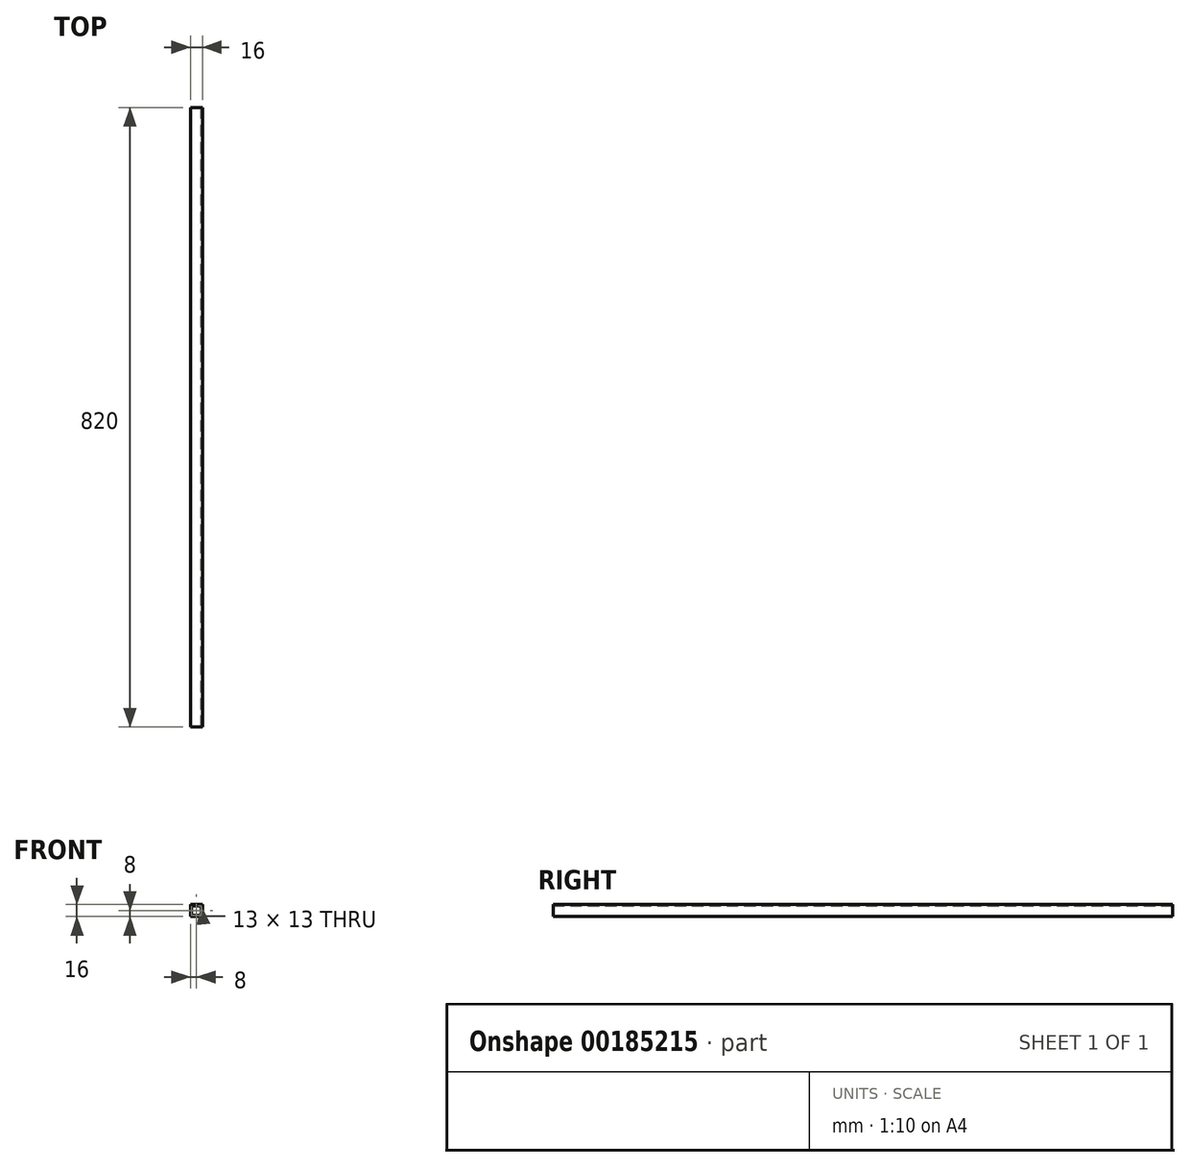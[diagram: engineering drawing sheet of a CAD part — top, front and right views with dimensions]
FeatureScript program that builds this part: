
annotation { "Feature Type Name" : "Feature", "Feature Type Description" : "" }
export const myFeature = defineFeature(function(context is Context, id is Id, definition is map)
    precondition{}
    {
        {
            var Q0;
            Q0=qCreatedBy(makeId("Front.planeOp"),FACE);
            var sketch = newSketch(context, id + "F0", { "sketchPlane" : qUnion([Q0])});
            skLineSegment(sketch, "E0.bottom", {"start": v(8, 8) * mm, "end": v(-8, 8) * mm});
            skLineSegment(sketch, "E0.top", {"start": v(8, -8) * mm, "end": v(-8, -8) * mm});
            skLineSegment(sketch, "E0.left", {"start": v(8, 8) * mm, "end": v(8, -8) * mm});
            skLineSegment(sketch, "E0.right", {"start": v(-8, 8) * mm, "end": v(-8, -8) * mm});
            skPoint(sketch, "E0.middle", {"position": v(0, 0) * mm});
            skLineSegment(sketch, "E1.0", {"start": v(6.5, 6.5) * mm, "end": v(-6.5, 6.5) * mm});
            skLineSegment(sketch, "E2.0", {"start": v(6.5, 6.5) * mm, "end": v(6.5, -6.5) * mm});
            skLineSegment(sketch, "E3.0", {"start": v(6.5, -6.5) * mm, "end": v(-6.5, -6.5) * mm});
            skLineSegment(sketch, "E4.0", {"start": v(-6.5, 6.5) * mm, "end": v(-6.5, -6.5) * mm});
            skSolve(sketch);
        }
        {
            var Q0;
            Q0=makeQuery(id+"F0.imprint","IMPRINT",FACE,{"disambiguationData":[TD([[makeQuery(id+"F0.imprint","IMPRINT",EDGE,{"derivedFrom":sQuery(id+"F0.wireOp",EDGE,"E0.bottom")}),1.0]])]});
            extrude(context, id + "F1", {"entities" : qUnion([Q0]), "depth" : 820 * mm, "offsetDistance" : 25 * mm});
        }
    });
